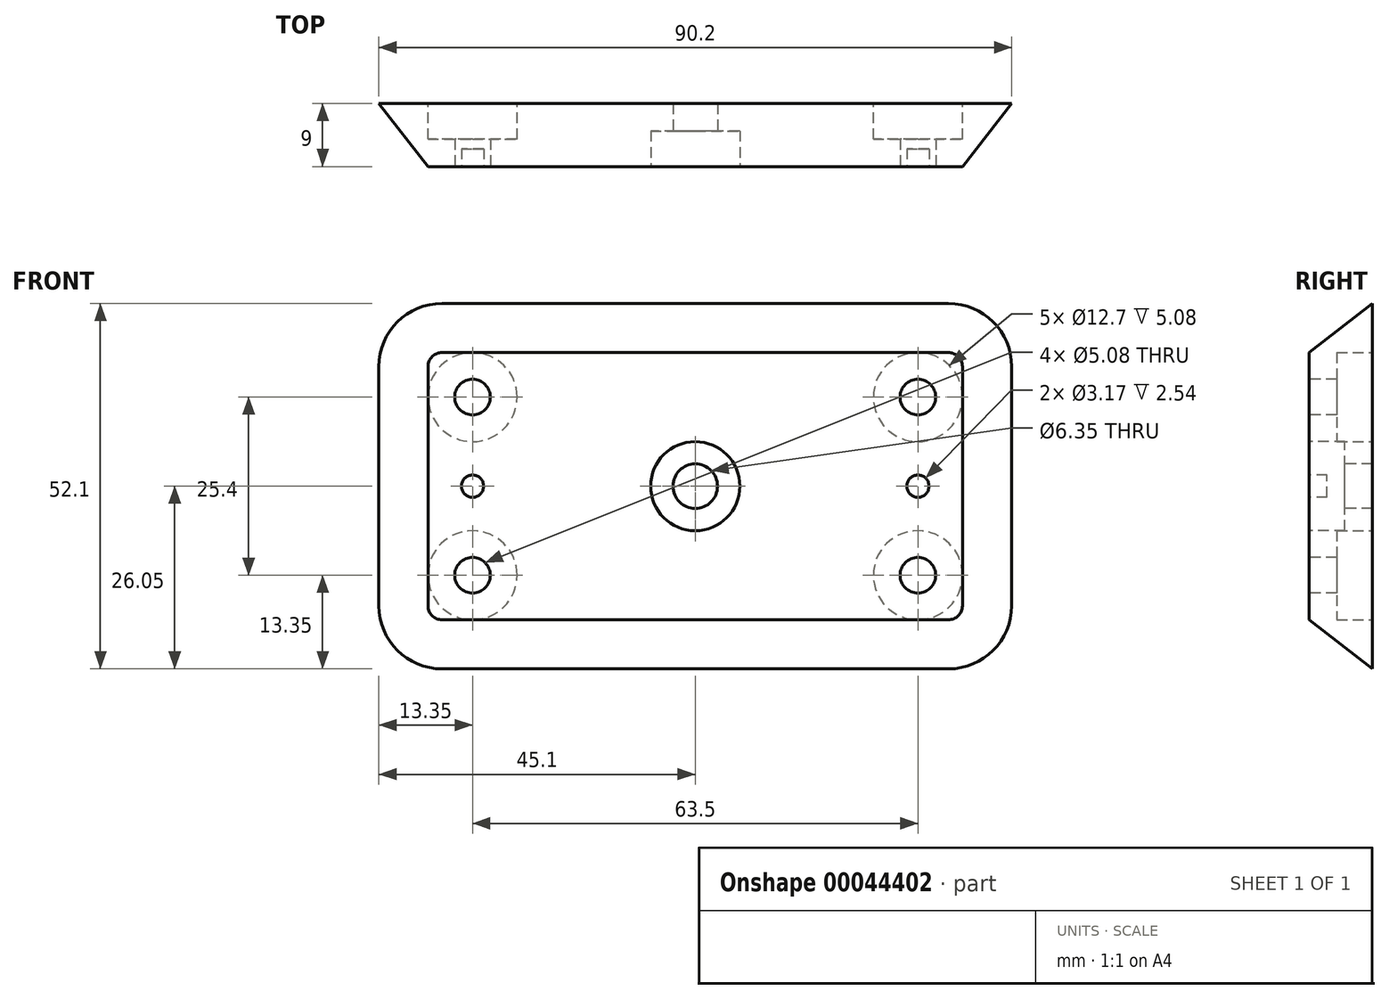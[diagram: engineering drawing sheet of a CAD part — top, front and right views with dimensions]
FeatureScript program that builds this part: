
annotation { "Feature Type Name" : "Feature", "Feature Type Description" : "" }
export const myFeature = defineFeature(function(context is Context, id is Id, definition is map)
    precondition{}
    {
        {
            var Q0;
            Q0=qCreatedBy(makeId("Front.planeOp"),FACE);
            var sketch = newSketch(context, id + "F0", { "sketchPlane" : qUnion([Q0])});
            skPoint(sketch, "E0.rect.middle", {"position": v(0, 0) * mm});
            skCircle(sketch, "E1", {"center": v(-31.75, 12.7) * mm, "radius": 2.54 * mm});
            skCircle(sketch, "E2", {"center": v(31.75, 12.7) * mm, "radius": 2.54 * mm});
            skCircle(sketch, "E3", {"center": v(-31.75, -12.7) * mm, "radius": 2.54 * mm});
            skCircle(sketch, "E4", {"center": v(31.75, -12.7) * mm, "radius": 2.54 * mm});
            skLineSegment(sketch, "E5", {"start": v(-31.75, 12.7) * mm, "end": v(31.75, 12.7) * mm, "construction": true});
            skPoint(sketch, "E6", {"position": v(0, 12.7) * mm});
            skLineSegment(sketch, "E7", {"start": v(31.75, 12.7) * mm, "end": v(31.75, -12.7) * mm, "construction": true});
            skPoint(sketch, "E8", {"position": v(31.75, 0) * mm});
            skCircle(sketch, "E9", {"center": v(0, 0) * mm, "radius": 3.18 * mm});
            skSolve(sketch);
        }
        {
            var Q0;
            Q0=qCreatedBy(makeId("Front.planeOp"),FACE);
            var sketch = newSketch(context, id + "F1", { "sketchPlane" : qUnion([Q0])});
            skLineSegment(sketch, "E10.rect.bottom", {"start": v(36.1, 19.05) * mm, "end": v(-36.1, 19.05) * mm});
            skLineSegment(sketch, "E10.rect.top", {"start": v(36.1, -19.05) * mm, "end": v(-36.1, -19.05) * mm});
            skLineSegment(sketch, "E10.rect.left", {"start": v(38.1, 17.05) * mm, "end": v(38.1, -17.05) * mm});
            skLineSegment(sketch, "E10.rect.right", {"start": v(-38.1, 17.05) * mm, "end": v(-38.1, -17.05) * mm});
            skPoint(sketch, "E10.rect.middle", {"position": v(0, 0) * mm});
            skPoint(sketch, "E11.visualSharp", {"position": v(-38.1, 19.05) * mm});
            skArc(sketch, "E11.filletArc", {"start": v(-36.1, 19.05) * mm, "mid": v(-37.51, 18.46) * mm, "end": v(-38.1, 17.05) * mm});
            skPoint(sketch, "E12.visualSharp", {"position": v(-38.1, -19.05) * mm});
            skArc(sketch, "E12.filletArc", {"start": v(-38.1, -17.05) * mm, "mid": v(-37.51, -18.46) * mm, "end": v(-36.1, -19.05) * mm});
            skPoint(sketch, "E13.visualSharp", {"position": v(38.1, -19.05) * mm});
            skArc(sketch, "E13.filletArc", {"start": v(36.1, -19.05) * mm, "mid": v(37.51, -18.46) * mm, "end": v(38.1, -17.05) * mm});
            skPoint(sketch, "E14.visualSharp", {"position": v(38.1, 19.05) * mm});
            skArc(sketch, "E14.filletArc", {"start": v(38.1, 17.05) * mm, "mid": v(37.51, 18.46) * mm, "end": v(36.1, 19.05) * mm});
            skSolve(sketch);
        }
        {
            var Q0;
            Q0=qCreatedBy(makeId("Front.planeOp"),FACE);
            cPlane(context, id + "F2", {"entities" : qUnion([Q0]), "cplaneType" : CPlaneType.OFFSET, "offset" : 9 * mm, "oppositeDirection" : true, "width" : 150 * mm, "height" : 150 * mm});
        }
        {
            var Q0;
            Q0=qCreatedBy(id+"F2.planeOp",FACE);
            var sketch = newSketch(context, id + "F3", { "sketchPlane" : qUnion([Q0])});
            skLineSegment(sketch, "E15.0", {"start": v(36.1, 19.05) * mm, "end": v(-36.1, 19.05) * mm, "construction": true});
            skLineSegment(sketch, "E15.1", {"start": v(36.1, -19.05) * mm, "end": v(-36.1, -19.05) * mm, "construction": true});
            skLineSegment(sketch, "E15.2", {"start": v(38.1, 17.05) * mm, "end": v(38.1, -17.05) * mm, "construction": true});
            skLineSegment(sketch, "E15.3", {"start": v(-38.1, 17.05) * mm, "end": v(-38.1, -17.05) * mm, "construction": true});
            skPoint(sketch, "E15.4", {"position": v(0, 0) * mm});
            skPoint(sketch, "E15.5", {"position": v(-38.1, 19.05) * mm});
            skArc(sketch, "E15.6", {"start": v(-36.1, 19.05) * mm, "mid": v(-37.51, 18.46) * mm, "end": v(-38.1, 17.05) * mm, "construction": true});
            skPoint(sketch, "E15.7", {"position": v(-38.1, -19.05) * mm});
            skArc(sketch, "E15.8", {"start": v(-38.1, -17.05) * mm, "mid": v(-37.51, -18.46) * mm, "end": v(-36.1, -19.05) * mm, "construction": true});
            skPoint(sketch, "E15.9", {"position": v(38.1, -19.05) * mm});
            skArc(sketch, "E15.10", {"start": v(36.1, -19.05) * mm, "mid": v(37.51, -18.46) * mm, "end": v(38.1, -17.05) * mm, "construction": true});
            skPoint(sketch, "E15.11", {"position": v(38.1, 19.05) * mm});
            skArc(sketch, "E15.12", {"start": v(38.1, 17.05) * mm, "mid": v(37.51, 18.46) * mm, "end": v(36.1, 19.05) * mm, "construction": true});
            skArc(sketch, "E16.0", {"start": v(-36.1, 26.05) * mm, "mid": v(-42.46, 23.41) * mm, "end": v(-45.1, 17.05) * mm});
            skLineSegment(sketch, "E16.1", {"start": v(36.1, 26.05) * mm, "end": v(-36.1, 26.05) * mm});
            skLineSegment(sketch, "E16.2", {"start": v(-45.1, 17.05) * mm, "end": v(-45.1, -17.05) * mm});
            skArc(sketch, "E16.3", {"start": v(45.1, 17.05) * mm, "mid": v(42.46, 23.41) * mm, "end": v(36.1, 26.05) * mm});
            skArc(sketch, "E16.4", {"start": v(-45.1, -17.05) * mm, "mid": v(-42.46, -23.41) * mm, "end": v(-36.1, -26.05) * mm});
            skLineSegment(sketch, "E16.5", {"start": v(36.1, -26.05) * mm, "end": v(-36.1, -26.05) * mm});
            skArc(sketch, "E16.6", {"start": v(36.1, -26.05) * mm, "mid": v(42.46, -23.41) * mm, "end": v(45.1, -17.05) * mm});
            skLineSegment(sketch, "E16.7", {"start": v(45.1, 17.05) * mm, "end": v(45.1, -17.05) * mm});
            skSolve(sketch);
        }
        {
            var Q0;
            Q0=makeQuery(id+"F1.imprint","IMPRINT",FACE,{"disambiguationData":[TD([[makeQuery(id+"F1.imprint","IMPRINT",EDGE,{"derivedFrom":sQuery(id+"F1.wireOp",EDGE,"E10.rect.bottom")}),1.0]])]});
            var Q1;
            Q1=makeQuery(id+"F3.imprint","IMPRINT",FACE,{"disambiguationData":[TD([[makeQuery(id+"F3.imprint","IMPRINT",EDGE,{"derivedFrom":sQuery(id+"F3.wireOp",EDGE,"E16.0")}),1.0]])]});
            loft(context, id + "F4", {"sheetProfilesArray" : [{ "sheetProfileEntities" : qUnion([Q0]) }, { "sheetProfileEntities" : qUnion([Q1]) }]});
        }
        {
            var Q0;
            Q0=makeQuery(id+"F0.imprint","IMPRINT",FACE,{"disambiguationData":[TD([[makeQuery(id+"F0.imprint","IMPRINT",EDGE,{"derivedFrom":sQuery(id+"F0.wireOp",EDGE,"E4")}),1.0]])]});
            var Q1;
            Q1=makeQuery(id+"F0.imprint","IMPRINT",FACE,{"disambiguationData":[TD([[makeQuery(id+"F0.imprint","IMPRINT",EDGE,{"derivedFrom":sQuery(id+"F0.wireOp",EDGE,"E2")}),1.0]])]});
            var Q2;
            Q2=makeQuery(id+"F0.imprint","IMPRINT",FACE,{"disambiguationData":[TD([[makeQuery(id+"F0.imprint","IMPRINT",EDGE,{"derivedFrom":sQuery(id+"F0.wireOp",EDGE,"E3")}),1.0]])]});
            var Q3;
            Q3=makeQuery(id+"F0.imprint","IMPRINT",FACE,{"disambiguationData":[TD([[makeQuery(id+"F0.imprint","IMPRINT",EDGE,{"derivedFrom":sQuery(id+"F0.wireOp",EDGE,"E1")}),1.0]])]});
            var Q4;
            Q4=makeQuery(id+"F0.imprint","IMPRINT",FACE,{"disambiguationData":[TD([[makeQuery(id+"F0.imprint","IMPRINT",EDGE,{"derivedFrom":sQuery(id+"F0.wireOp",EDGE,"E9")}),1.0]])]});
            extrude(context, id + "F5", {"entities" : qUnion([Q0, Q1, Q2, Q3, Q4]), "operationType" : NewBodyOperationType.REMOVE, "endBound" : BoundingType.UP_TO_NEXT, "oppositeDirection" : true, "depth" : 25 * mm});
        }
        {
            var Q0;
            Q0=makeQuery(id+"F4.opLoft","CAP_FACE",FACE,{"disambiguationData":[OSD([makeQuery(id+"F1.imprint","IMPRINT",FACE,{"disambiguationData":[TD([[makeQuery(id+"F1.imprint","IMPRINT",EDGE,{"derivedFrom":sQuery(id+"F1.wireOp",EDGE,"E10.rect.bottom")}),1.0]])]})])],"isStart":true});
            var sketch = newSketch(context, id + "F6", { "sketchPlane" : qUnion([Q0])});
            skCircle(sketch, "E17", {"center": v(31.75, 0) * mm, "radius": 1.59 * mm});
            skCircle(sketch, "E18", {"center": v(-31.75, 0) * mm, "radius": 1.59 * mm});
            skSolve(sketch);
        }
        {
            var Q0;
            Q0=makeQuery(id+"F6.imprint","IMPRINT",FACE,{"disambiguationData":[TD([[makeQuery(id+"F6.imprint","IMPRINT",EDGE,{"derivedFrom":sQuery(id+"F6.wireOp",EDGE,"E17")}),1.0]])]});
            var Q1;
            Q1=makeQuery(id+"F6.imprint","IMPRINT",FACE,{"disambiguationData":[TD([[makeQuery(id+"F6.imprint","IMPRINT",EDGE,{"derivedFrom":sQuery(id+"F6.wireOp",EDGE,"E18")}),1.0]])]});
            extrude(context, id + "F7", {"entities" : qUnion([Q0, Q1]), "operationType" : NewBodyOperationType.REMOVE, "oppositeDirection" : true, "depth" : 2.54 * mm});
        }
        {
            var Q0;
            Q0=makeQuery(id+"F4.opLoft","CAP_FACE",FACE,{"disambiguationData":[OSD([makeQuery(id+"F1.imprint","IMPRINT",FACE,{"disambiguationData":[TD([[makeQuery(id+"F1.imprint","IMPRINT",EDGE,{"derivedFrom":sQuery(id+"F1.wireOp",EDGE,"E10.rect.bottom")}),1.0]])]})])],"isStart":true});
            var sketch = newSketch(context, id + "F8", { "sketchPlane" : qUnion([Q0])});
            skCircle(sketch, "E19", {"center": v(0, 0) * mm, "radius": 6.35 * mm});
            skSolve(sketch);
        }
        {
            var Q0;
            Q0 = qSketchRegion(id + "F8", true);
            extrude(context, id + "F9", {"entities" : qUnion([Q0]), "operationType" : NewBodyOperationType.REMOVE, "oppositeDirection" : true, "depth" : 5.08 * mm});
        }
        {
            var Q0;
            Q0=makeQuery(id+"F4.opLoft","CAP_FACE",FACE,{"disambiguationData":[OSD([makeQuery(id+"F3.imprint","IMPRINT",FACE,{"disambiguationData":[TD([[makeQuery(id+"F3.imprint","IMPRINT",EDGE,{"derivedFrom":sQuery(id+"F3.wireOp",EDGE,"E16.0")}),1.0]])]})])],"isStart":true});
            var sketch = newSketch(context, id + "F10", { "sketchPlane" : qUnion([Q0])});
            skCircle(sketch, "E20", {"center": v(-31.75, 12.7) * mm, "radius": 6.35 * mm});
            skCircle(sketch, "E21", {"center": v(-31.75, -12.7) * mm, "radius": 6.35 * mm});
            skCircle(sketch, "E22", {"center": v(31.75, 12.7) * mm, "radius": 6.35 * mm});
            skCircle(sketch, "E23", {"center": v(31.75, -12.7) * mm, "radius": 6.35 * mm});
            skSolve(sketch);
        }
        {
            var Q0;
            Q0 = qSketchRegion(id + "F10", true);
            extrude(context, id + "F11", {"entities" : qUnion([Q0]), "operationType" : NewBodyOperationType.REMOVE, "oppositeDirection" : true, "depth" : 5.08 * mm});
        }
    });
